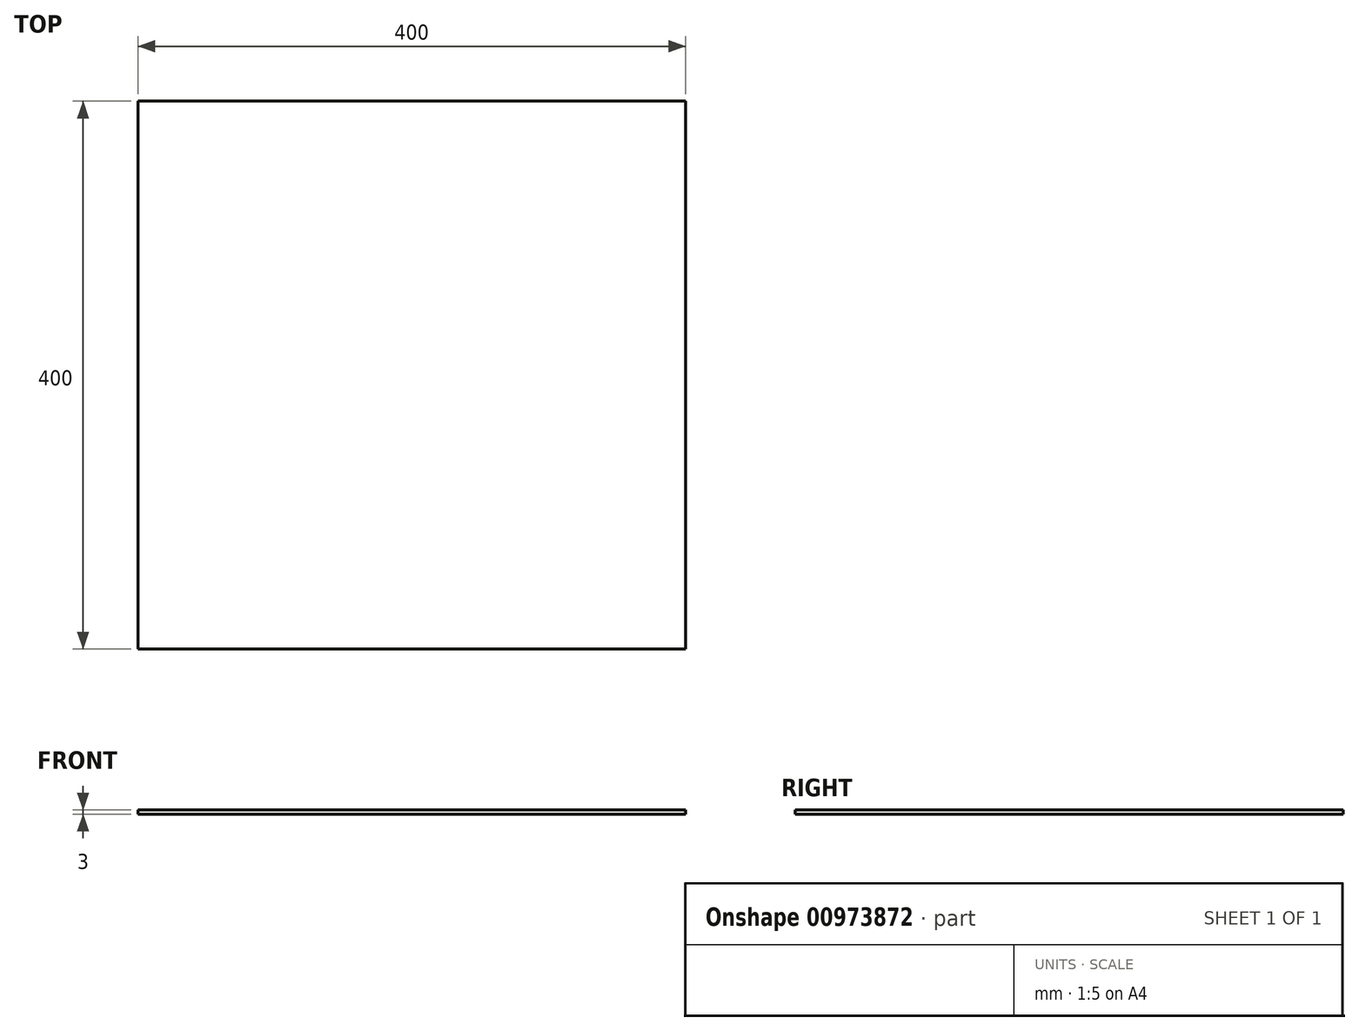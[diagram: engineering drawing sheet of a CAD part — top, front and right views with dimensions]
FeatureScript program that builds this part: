
annotation { "Feature Type Name" : "Feature", "Feature Type Description" : "" }
export const myFeature = defineFeature(function(context is Context, id is Id, definition is map)
    precondition{}
    {
        {
            var Q0;
            Q0=qCreatedBy(makeId("Front.planeOp"),FACE);
            var sketch = newSketch(context, id + "F0", { "sketchPlane" : qUnion([Q0])});
            skLineSegment(sketch, "E0.bottom", {"start": v(60, 30) * mm, "end": v(-60, 30) * mm});
            skLineSegment(sketch, "E0.top", {"start": v(60, -30) * mm, "end": v(-60, -30) * mm});
            skLineSegment(sketch, "E0.left", {"start": v(60, 30) * mm, "end": v(60, -30) * mm});
            skLineSegment(sketch, "E0.right", {"start": v(-60, 30) * mm, "end": v(-60, -30) * mm});
            skPoint(sketch, "E0.middle", {"position": v(0, 0) * mm});
            skSolve(sketch);
        }
        {
            var Q0;
            Q0 = qSketchRegion(id + "F0", true);
            extrude(context, id + "F1", {"entities" : qUnion([Q0]), "depth" : 100 * mm, "offsetDistance" : 25 * mm});
        }
        {
            var Q0;
            Q0=makeQuery(id+"F1.opExtrude","SWEPT_BODY",BODY,{"disambiguationData":[OSD([sQuery(id+"F0.wireOp",EDGE,"E0.bottom"),sQuery(id+"F0.wireOp",EDGE,"E0.top"),sQuery(id+"F0.wireOp",EDGE,"E0.left"),sQuery(id+"F0.wireOp",EDGE,"E0.right")])]});
            deleteBodies(context, id + "F2", {"entities" : qUnion([Q0])});
        }
        {
            var Q0;
            Q0=qCreatedBy(makeId("Top.planeOp"),FACE);
            var sketch = newSketch(context, id + "F3", { "sketchPlane" : qUnion([Q0])});
            skLineSegment(sketch, "E1.bottom", {"start": v(-200, 200) * mm, "end": v(200, 200) * mm});
            skLineSegment(sketch, "E1.top", {"start": v(-200, -200) * mm, "end": v(200, -200) * mm});
            skLineSegment(sketch, "E1.left", {"start": v(-200, 200) * mm, "end": v(-200, -200) * mm});
            skLineSegment(sketch, "E1.right", {"start": v(200, 200) * mm, "end": v(200, -200) * mm});
            skPoint(sketch, "E1.middle", {"position": v(0, 0) * mm});
            skSolve(sketch);
        }
        {
            var Q0;
            Q0 = qSketchRegion(id + "F3", true);
            extrude(context, id + "F4", {"entities" : qUnion([Q0]), "depth" : 3 * mm, "offsetDistance" : 25 * mm});
        }
        {
            var Q0;
            Q0=makeQuery(id+"F4.opExtrude","SWEPT_BODY",BODY,{"disambiguationData":[OSD([sQuery(id+"F3.wireOp",EDGE,"E1.bottom"),sQuery(id+"F3.wireOp",EDGE,"E1.top"),sQuery(id+"F3.wireOp",EDGE,"E1.left"),sQuery(id+"F3.wireOp",EDGE,"E1.right")])]});
            deleteBodies(context, id + "F5", {"entities" : qUnion([Q0])});
        }
        {
            var Q0;
            Q0=qCreatedBy(makeId("Top.planeOp"),FACE);
            var sketch = newSketch(context, id + "F6", { "sketchPlane" : qUnion([Q0])});
            skLineSegment(sketch, "E2.bottom", {"start": v(200, -200) * mm, "end": v(-200, -200) * mm});
            skLineSegment(sketch, "E2.top", {"start": v(200, 200) * mm, "end": v(-200, 200) * mm});
            skLineSegment(sketch, "E2.left", {"start": v(200, -200) * mm, "end": v(200, 200) * mm});
            skLineSegment(sketch, "E2.right", {"start": v(-200, -200) * mm, "end": v(-200, 200) * mm});
            skPoint(sketch, "E2.middle", {"position": v(0, 0) * mm});
            skPoint(sketch, "E3.centerSnap0", {"position": v(0, -200) * mm});
            skSolve(sketch);
        }
        {
            var Q0;
            Q0 = qSketchRegion(id + "F6", true);
            extrude(context, id + "F7", {"entities" : qUnion([Q0]), "depth" : 3 * mm, "offsetDistance" : 25 * mm});
        }
    });
